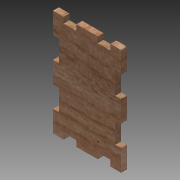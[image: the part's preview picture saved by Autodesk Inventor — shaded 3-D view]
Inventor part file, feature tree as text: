
AUTODESK INVENTOR PART (.ipt)
format: ipt  version: 2015 (Build 190159000, 159)  size: 242,176 bytes
history: native  units: mm
features: other x9, sketch x6, extrude x3
ambient origin geometry x8: Origin, YZ Plane, XZ Plane, XY Plane, X Axis, Y Axis, Z Axis, Center Point
bodies: Solid1 (feature_tree)
feature tree (18):
  other  "Blocks"
  extrude  "Extrusion1"  Depth=100.0mm
  extrude  "Extrusion3"  TaperAngle=0.0deg  [1 undecoded]
  extrude  "Extrusion4"  Depth=20.0mm
  sketch  "Sketch15"  dims[d15=5.5mm]
  sketch  "Sketch16"  dims[d16=0.0mm d17=5.5mm d18=12.0mm d19=20.0mm d20=5.5mm d21=0.0mm]
  sketch  "Sketch14"  dims[d14=5.5mm]
  sketch  "Sketch1"  dims[d0=64.0mm d1=100.0mm]
  sketch  "Sketch5"  dims[d2=5.5mm d3=0.0mm]
  sketch  "Sketch6"  dims[d12=20.0mm d13=20.0mm]
  other  "Block1"
  other  "Block2"
  other  "Block3"
  other  "Block4"
  other  "Block3:1"
  other  "Block3:2"
  other  "Block4:1"
  other  "Block4:2"
note: 1 required parameter value undecoded (feature->parameter linkage not recoverable at this tier; creation-order binding heuristic only, values carry confidence <= 0.55)
